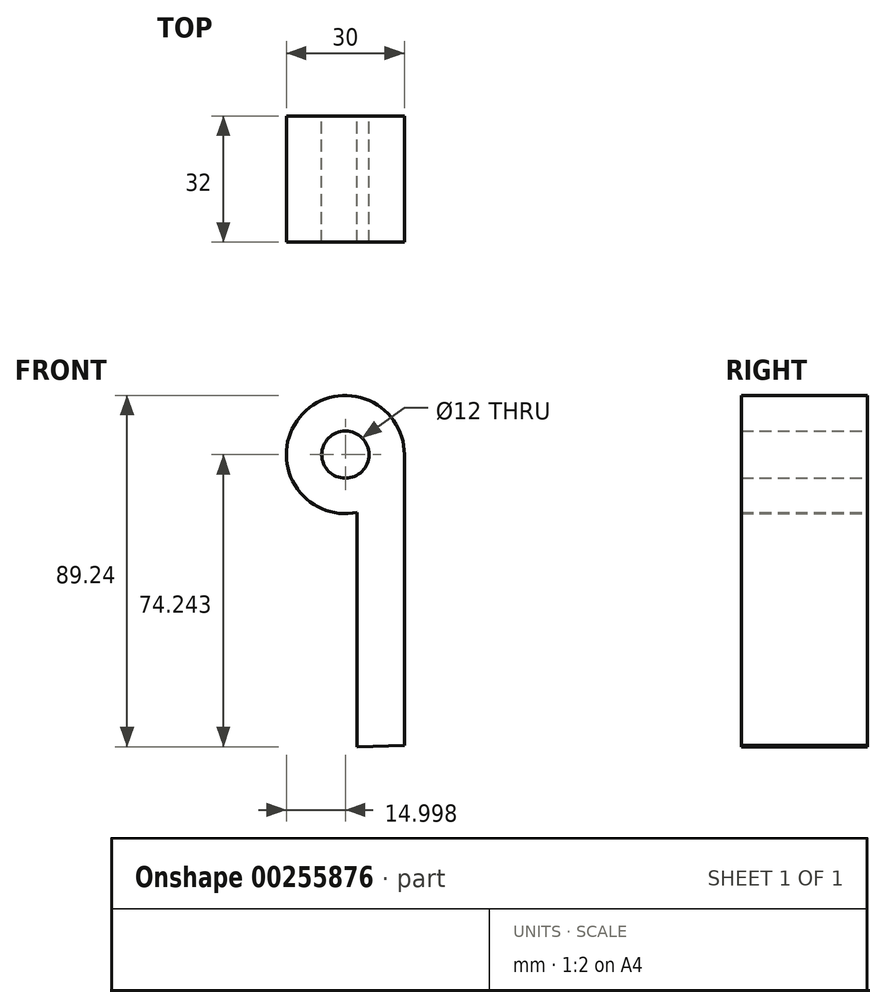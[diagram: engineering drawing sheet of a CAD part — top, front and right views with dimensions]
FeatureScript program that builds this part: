
annotation { "Feature Type Name" : "Feature", "Feature Type Description" : "" }
export const myFeature = defineFeature(function(context is Context, id is Id, definition is map)
    precondition{}
    {
        {
            var Q0;
            Q0=qCreatedBy(makeId("Front.planeOp"),FACE);
            var sketch = newSketch(context, id + "F0", { "sketchPlane" : qUnion([Q0])});
            skLineSegment(sketch, "E0.bottom", {"start": v(-6, -37.22) * mm, "end": v(6, -36.9) * mm});
            skLineSegment(sketch, "E0.left", {"start": v(-6, -37.22) * mm, "end": v(-6, 22.33) * mm});
            skLineSegment(sketch, "E0.right", {"start": v(6, -36.9) * mm, "end": v(6, 37.22) * mm});
            skPoint(sketch, "E0.middle", {"position": v(0, 0) * mm});
            skArc(sketch, "E1", {"start": v(6, 37.02) * mm, "mid": v(-20.62, 46.5) * mm, "end": v(-6, 22.33) * mm});
            skPoint(sketch, "E2.orphan", {"position": v(-6, 36.9) * mm});
            skLineSegment(sketch, "E3", {"start": v(6, 37.02) * mm, "end": v(6, 37.22) * mm});
            skCircle(sketch, "E4", {"center": v(-9, 37.02) * mm, "radius": 6 * mm});
            skSolve(sketch);
        }
        {
            var Q0;
            Q0=makeQuery(id+"F0.imprint","IMPRINT",FACE,{"disambiguationData":[TD([[makeQuery(id+"F0.imprint","IMPRINT",EDGE,{"derivedFrom":sQuery(id+"F0.wireOp",EDGE,"E0.bottom")}),1.0]])]});
            extrude(context, id + "F1", {"entities" : qUnion([Q0]), "depth" : 32 * mm});
        }
    });
